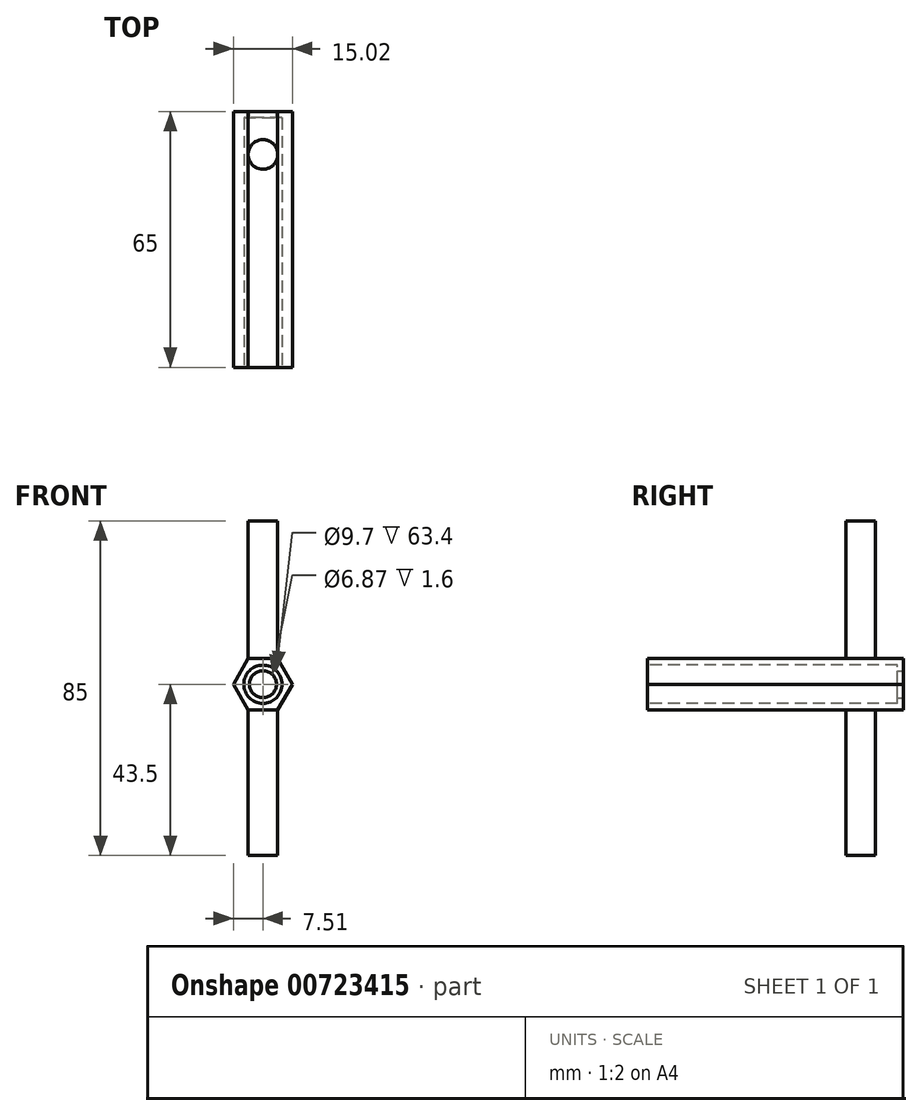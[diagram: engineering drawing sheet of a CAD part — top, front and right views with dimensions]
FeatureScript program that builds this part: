
annotation { "Feature Type Name" : "Feature", "Feature Type Description" : "" }
export const myFeature = defineFeature(function(context is Context, id is Id, definition is map)
    precondition{}
    {
        {
            var Q0;
            Q0=qCreatedBy(makeId("Front.planeOp"),FACE);
            var sketch = newSketch(context, id + "F0", { "sketchPlane" : qUnion([Q0])});
            skCircle(sketch, "E0.cCircle", {"center": v(0, 0) * mm, "radius": 6.5 * mm, "construction": true});
            skLineSegment(sketch, "E0.0", {"start": v(7.5, 0) * mm, "end": v(3.75, -6.5) * mm});
            skLineSegment(sketch, "E0.1", {"start": v(3.75, -6.5) * mm, "end": v(-3.76, -6.5) * mm});
            skLineSegment(sketch, "E0.2", {"start": v(-3.76, -6.5) * mm, "end": v(-7.5, 0) * mm});
            skLineSegment(sketch, "E0.3", {"start": v(-7.5, 0) * mm, "end": v(-3.75, 6.5) * mm});
            skLineSegment(sketch, "E0.4", {"start": v(-3.75, 6.5) * mm, "end": v(3.76, 6.5) * mm});
            skLineSegment(sketch, "E0.5", {"start": v(3.76, 6.5) * mm, "end": v(7.5, 0) * mm});
            skPoint(sketch, "E0.0.midPoint", {"position": v(5.63, -3.25) * mm});
            skSolve(sketch);
        }
        {
            var Q0;
            Q0=qSketchRegion(id+"F0",true);
            extrude(context, id + "F1", {"entities" : qUnion([Q0]), "endBound" : BoundingType.SYMMETRIC, "depth" : 65 * mm, "offsetDistance" : 25 * mm});
        }
        {
            var Q0;
            Q0=makeQuery(id+"F1.opExtrude","SWEPT_FACE",FACE,{"disambiguationData":[OSD([sQuery(id+"F0.wireOp",EDGE,"E0.4")])]});
            var sketch = newSketch(context, id + "F2", { "sketchPlane" : qUnion([Q0])});
            skCircle(sketch, "E1", {"center": v(0, 21.6) * mm, "radius": 3.75 * mm});
            skSolve(sketch);
        }
        {
            var Q0;
            Q0=makeQuery(id+"F2.imprint","IMPRINT",FACE,{"disambiguationData":[TD([[makeQuery(id+"F2.imprint","IMPRINT",EDGE,{"derivedFrom":sQuery(id+"F2.wireOp",EDGE,"E1")}),1.0]])]});
            extrude(context, id + "F3", {"entities" : qUnion([Q0]), "operationType" : NewBodyOperationType.ADD, "depth" : 35 * mm, "offsetDistance" : 25 * mm, "hasSecondDirection" : true, "secondDirectionOppositeDirection" : true, "secondDirectionDepth" : 50 * mm});
        }
        {
            var Q0;
            Q0=makeQuery(id+"F1.opExtrude","CAP_FACE",FACE,{"disambiguationData":[OSD([sQuery(id+"F0.wireOp",EDGE,"E0.0"),sQuery(id+"F0.wireOp",EDGE,"E0.1"),sQuery(id+"F0.wireOp",EDGE,"E0.2"),sQuery(id+"F0.wireOp",EDGE,"E0.3"),sQuery(id+"F0.wireOp",EDGE,"E0.4"),sQuery(id+"F0.wireOp",EDGE,"E0.5")])],"isStart":false});
            var sketch = newSketch(context, id + "F4", { "sketchPlane" : qUnion([Q0])});
            skCircle(sketch, "E2", {"center": v(0, 0) * mm, "radius": 4.85 * mm});
            skSolve(sketch);
        }
        {
            var Q0;
            Q0=makeQuery(id+"F4.imprint","IMPRINT",FACE,{"disambiguationData":[TD([[makeQuery(id+"F4.imprint","IMPRINT",EDGE,{"derivedFrom":sQuery(id+"F4.wireOp",EDGE,"E2")}),1.0]])]});
            var Q1;
            Q1 = qSketchRegion(id + "F4", true);
            extrude(context, id + "F5", {"entities" : qUnion([Q0, Q1]), "operationType" : NewBodyOperationType.REMOVE, "oppositeDirection" : true, "depth" : 63.4 * mm, "offsetDistance" : 25 * mm});
        }
        {
            var Q0;
            Q0=makeQuery(id+"F1.opExtrude","CAP_FACE",FACE,{"disambiguationData":[OSD([sQuery(id+"F0.wireOp",EDGE,"E0.0"),sQuery(id+"F0.wireOp",EDGE,"E0.1"),sQuery(id+"F0.wireOp",EDGE,"E0.2"),sQuery(id+"F0.wireOp",EDGE,"E0.3"),sQuery(id+"F0.wireOp",EDGE,"E0.4"),sQuery(id+"F0.wireOp",EDGE,"E0.5")])],"isStart":true});
            var sketch = newSketch(context, id + "F6", { "sketchPlane" : qUnion([Q0])});
            skCircle(sketch, "E3", {"center": v(0, 0) * mm, "radius": 3.43 * mm});
            skSolve(sketch);
        }
        {
            var Q0;
            Q0=makeQuery(id+"F6.imprint","IMPRINT",FACE,{"disambiguationData":[TD([[makeQuery(id+"F6.imprint","IMPRINT",EDGE,{"derivedFrom":sQuery(id+"F6.wireOp",EDGE,"E3")}),1.0]])]});
            extrude(context, id + "F7", {"entities" : qUnion([Q0]), "operationType" : NewBodyOperationType.REMOVE, "oppositeDirection" : true, "depth" : 90 * mm, "offsetDistance" : 25 * mm});
        }
    });
